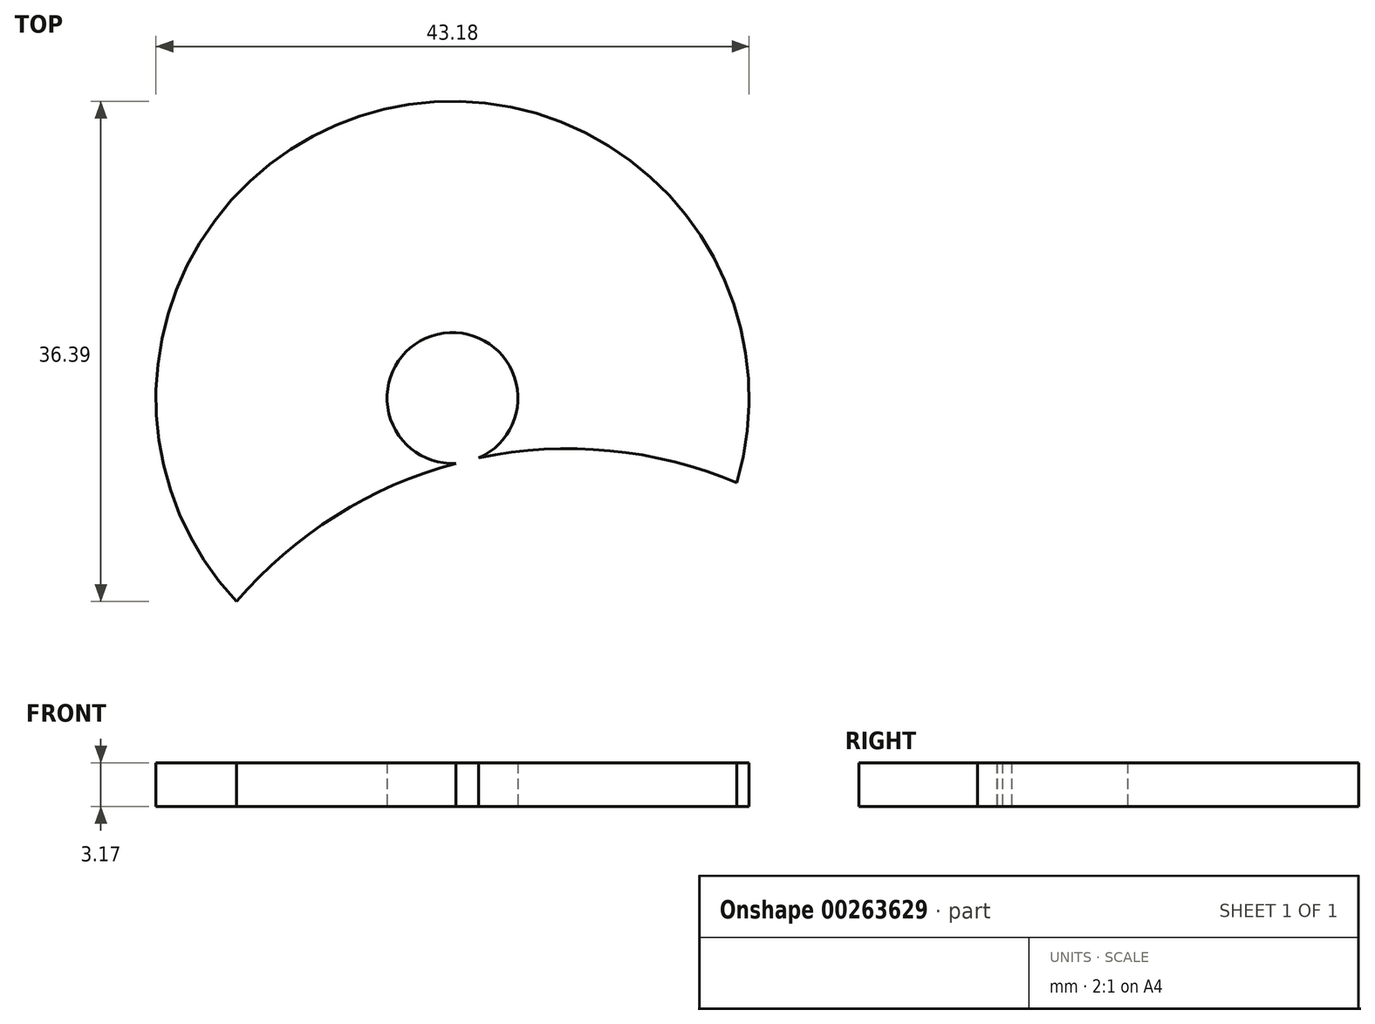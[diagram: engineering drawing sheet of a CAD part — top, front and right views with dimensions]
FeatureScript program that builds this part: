
annotation { "Feature Type Name" : "Feature", "Feature Type Description" : "" }
export const myFeature = defineFeature(function(context is Context, id is Id, definition is map)
    precondition{}
    {
        {
            var Q0;
            Q0=qCreatedBy(makeId("Top.planeOp"),FACE);
            var sketch = newSketch(context, id + "F0", { "sketchPlane" : qUnion([Q0])});
            skArc(sketch, "E0", {"start": v(20.7, -6.16) * mm, "mid": v(-4.99, 21) * mm, "end": v(-15.71, -14.8) * mm});
            skArc(sketch, "E1", {"start": v(20.7, -6.16) * mm, "mid": v(1.08, -4.55) * mm, "end": v(-15.71, -14.8) * mm});
            skCircle(sketch, "E2", {"center": v(0, 0) * mm, "radius": 4.76 * mm});
            skSolve(sketch);
        }
        {
            var Q0;
            Q0=makeQuery(id+"F0.imprint","IMPRINT",FACE,{"disambiguationData":[TD([[makeQuery(id+"F0.imprint","IMPRINT",EDGE,{"derivedFrom":sQuery(id+"F0.wireOp",EDGE,"E0")}),1.0]])]});
            extrude(context, id + "F1", {"entities" : qUnion([Q0]), "depth" : 3.17 * mm});
        }
    });
